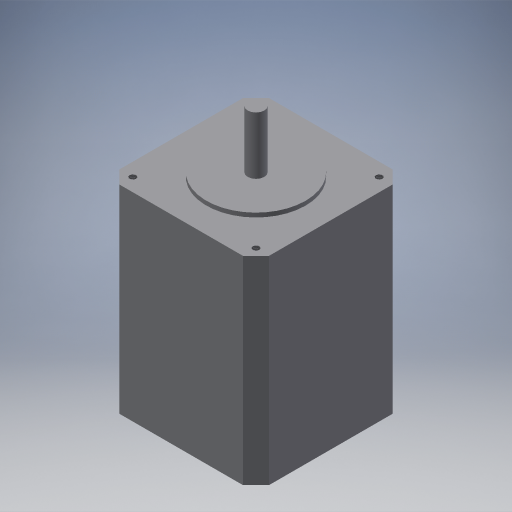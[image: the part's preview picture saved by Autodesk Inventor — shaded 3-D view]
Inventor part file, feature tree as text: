
AUTODESK INVENTOR PART (.ipt)
format: ipt  version: 2024.3 (Build 283343000, 343)  size: 258,048 bytes
history: native  units: mm
features: extrude x3, sketch x3, hole x1, chamfer x1, projected_geometry x1
ambient origin geometry x8: Origin, YZ Plane, XZ Plane, XY Plane, X Axis, Y Axis, Z Axis, Center Point
bodies: Volumenkörper1 (feature_tree)
feature tree (9):
  extrude  "Extrusion1"  Depth=57.3mm
  extrude  "Extrusion2"  Depth=76.0mm
  extrude  "Extrusion3"  Depth=22.0mm
  hole  "Bohrung1"  [1 undecoded]
  chamfer  "Fasen1"  Distance=47.15mm
  sketch  "Skizze2"  dims[d0=57.3mm d1=57.3mm]
  sketch  "Skizze3"  dims[d2=76.0mm d3=0.0mm d4=38.0mm]
  sketch  "Skizze4"  dims[d5=1.6mm d6=0.0mm d7=6.35mm d8=22.0mm d9=0.0mm d10=47.15mm d11=47.15mm d12=2.459mm d13=6.0mm d14=6.0mm d15=2.0mm d16=90.0deg d17=8.8mm d18=20.594885mm d19=5.0mm d20=2.0mm d21=45.0deg]
  projected_geometry  "Projizierte Kontur1"
note: 1 required parameter value undecoded (feature->parameter linkage not recoverable at this tier; creation-order binding heuristic only, values carry confidence <= 0.55)
